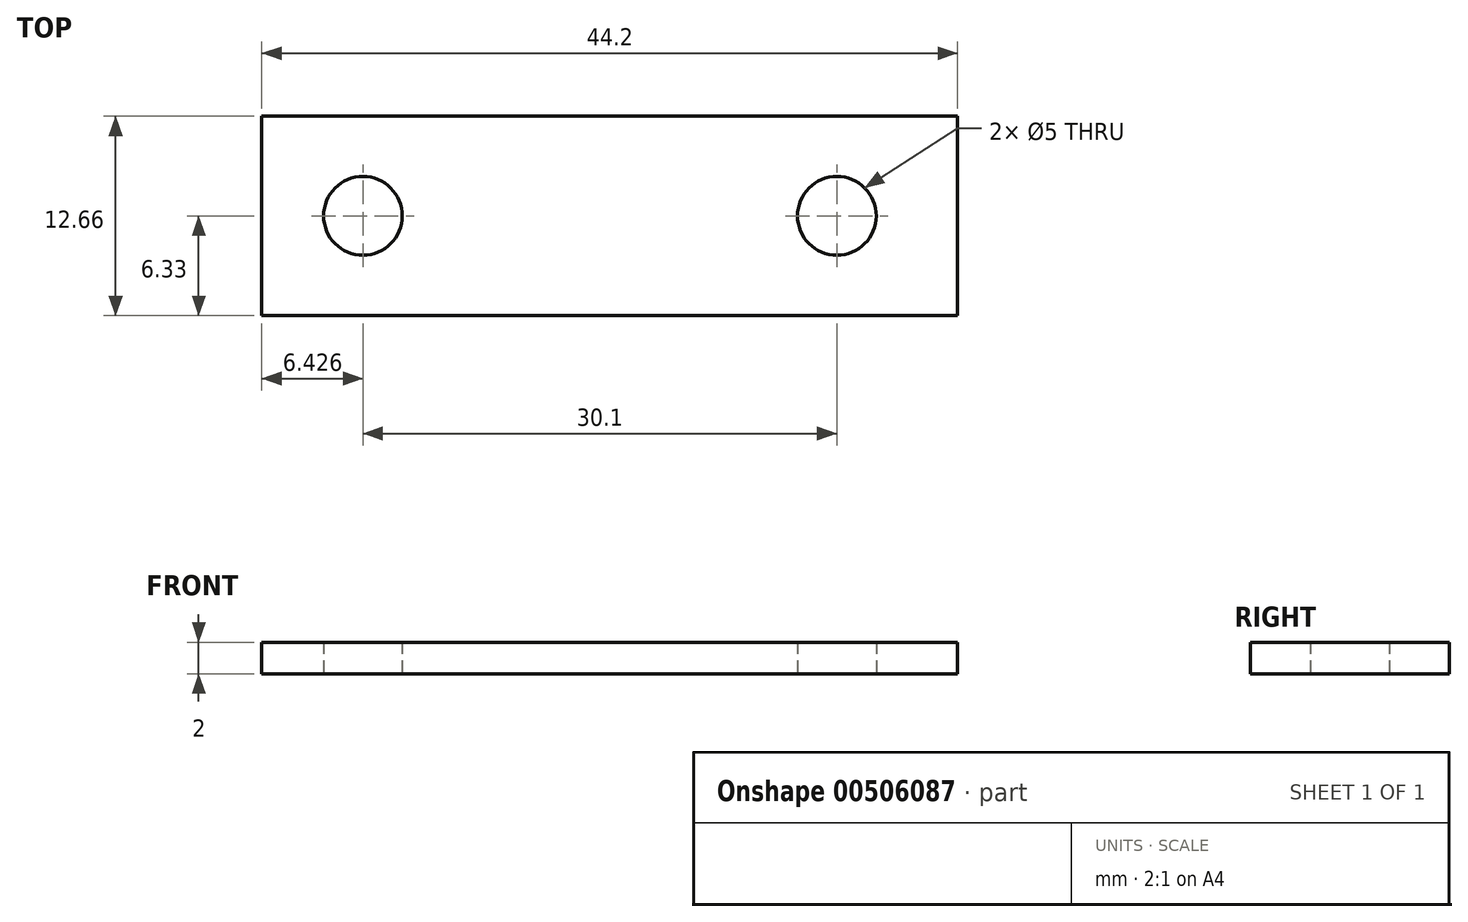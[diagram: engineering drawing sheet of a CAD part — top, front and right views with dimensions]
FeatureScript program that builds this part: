
annotation { "Feature Type Name" : "Feature", "Feature Type Description" : "" }
export const myFeature = defineFeature(function(context is Context, id is Id, definition is map)
    precondition{}
    {
        {
            var Q0;
            Q0=qCreatedBy(makeId("Top.planeOp"),FACE);
            var sketch = newSketch(context, id + "F0", { "sketchPlane" : qUnion([Q0])});
            skLineSegment(sketch, "E0.bottom", {"start": v(22.1, -6.33) * mm, "end": v(-22.1, -6.33) * mm});
            skLineSegment(sketch, "E0.top", {"start": v(22.1, 6.33) * mm, "end": v(-22.1, 6.32) * mm});
            skLineSegment(sketch, "E0.left", {"start": v(22.1, -6.32) * mm, "end": v(22.1, 6.33) * mm});
            skLineSegment(sketch, "E0.right", {"start": v(-22.1, -6.33) * mm, "end": v(-22.1, 6.32) * mm});
            skPoint(sketch, "E0.middle", {"position": v(0, 0) * mm});
            skCircle(sketch, "E1", {"center": v(14.43, 0) * mm, "radius": 2.5 * mm});
            skCircle(sketch, "E2", {"center": v(-15.67, 0) * mm, "radius": 2.5 * mm});
            skSolve(sketch);
        }
        {
            var Q0;
            Q0=makeQuery(id+"F0.imprint","IMPRINT",FACE,{"disambiguationData":[TD([[makeQuery(id+"F0.imprint","IMPRINT",EDGE,{"derivedFrom":sQuery(id+"F0.wireOp",EDGE,"E0.bottom")}),-1.0]])]});
            extrude(context, id + "F1", {"entities" : qUnion([Q0]), "depth" : 2 * mm});
        }
    });
